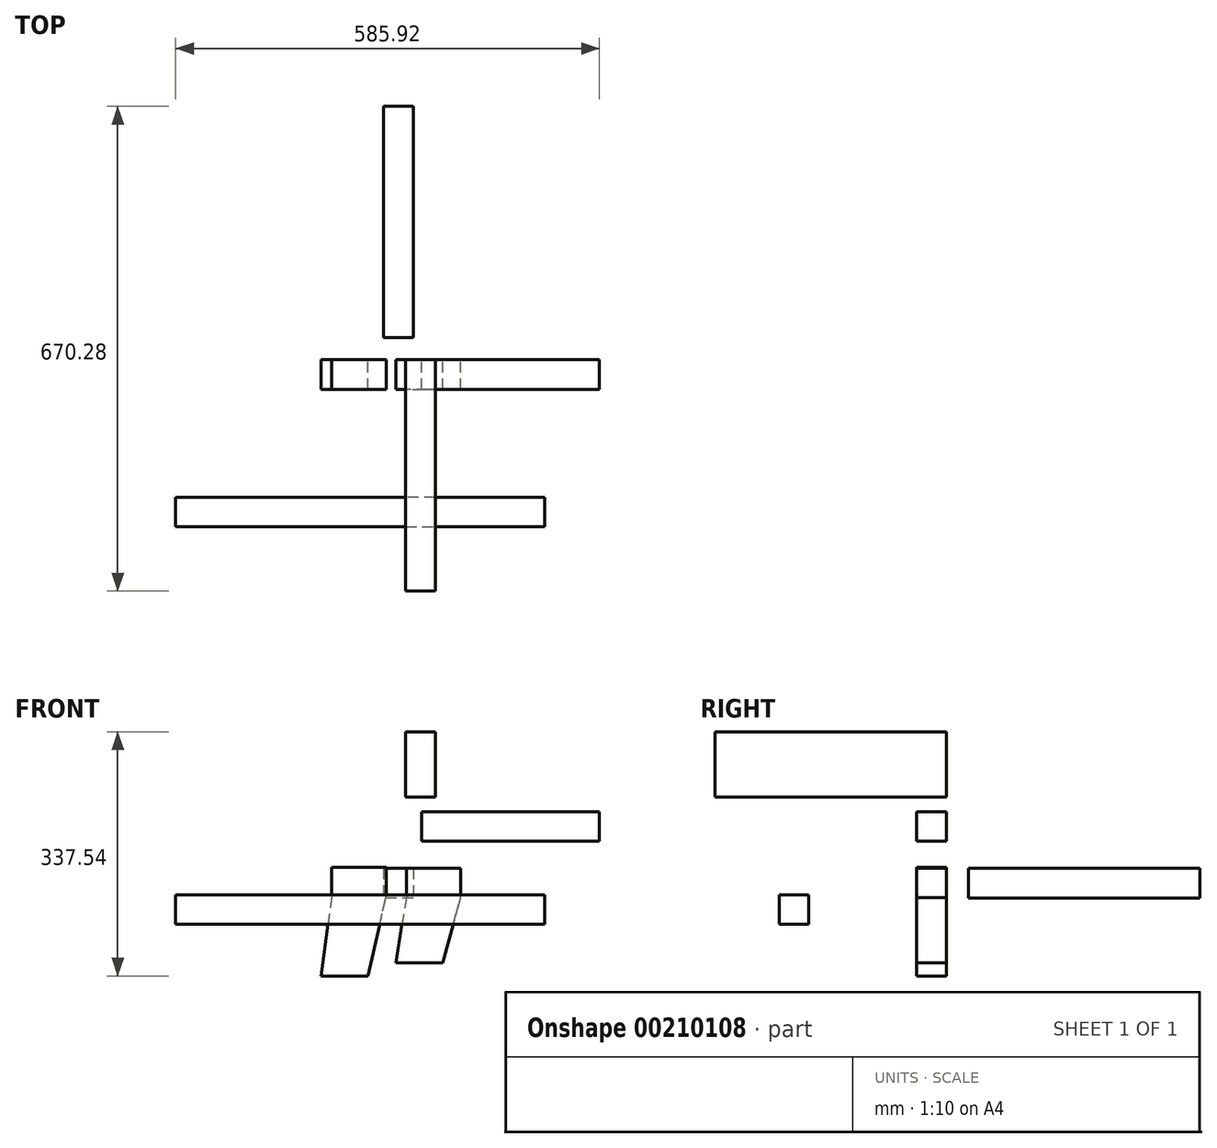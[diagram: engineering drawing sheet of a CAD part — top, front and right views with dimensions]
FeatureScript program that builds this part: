
annotation { "Feature Type Name" : "Feature", "Feature Type Description" : "" }
export const myFeature = defineFeature(function(context is Context, id is Id, definition is map)
    precondition{}
    {
        {
            var Q0;
            Q0=qCreatedBy(makeId("Front.planeOp"),FACE);
            var sketch = newSketch(context, id + "F0", { "sketchPlane" : qUnion([Q0])});
            skLineSegment(sketch, "E0", {"start": v(-71.59, 78.64) * mm, "end": v(-71.59, 37.64) * mm});
            skLineSegment(sketch, "E1", {"start": v(-71.59, 37.64) * mm, "end": v(-86.59, -71.36) * mm});
            skLineSegment(sketch, "E2", {"start": v(-86.59, -71.36) * mm, "end": v(-21.65, -71.36) * mm});
            skLineSegment(sketch, "E3", {"start": v(-21.65, -71.36) * mm, "end": v(3.41, 37.64) * mm});
            skLineSegment(sketch, "E4", {"start": v(3.41, 37.64) * mm, "end": v(3.41, 78.64) * mm});
            skLineSegment(sketch, "E5", {"start": v(3.41, 78.64) * mm, "end": v(-71.59, 78.64) * mm});
            skSolve(sketch);
        }
        {
            var Q0;
            Q0=qSketchRegion(id+"F0",true);
            extrude(context, id + "F1", {"entities" : qUnion([Q0]), "depth" : 41 * mm});
        }
        {
            var Q0;
            Q0=qCreatedBy(makeId("Front.planeOp"),FACE);
            var sketch = newSketch(context, id + "F2", { "sketchPlane" : qUnion([Q0])});
            skLineSegment(sketch, "E6", {"start": v(52.4, 155.86) * mm, "end": v(52.4, 114.86) * mm});
            skLineSegment(sketch, "E7", {"start": v(52.4, 114.86) * mm, "end": v(298.4, 114.86) * mm});
            skLineSegment(sketch, "E8", {"start": v(298.4, 114.86) * mm, "end": v(298.4, 155.86) * mm});
            skLineSegment(sketch, "E9", {"start": v(298.4, 155.86) * mm, "end": v(52.4, 155.86) * mm});
            skSolve(sketch);
        }
        {
            var Q0;
            Q0=qSketchRegion(id+"F2",true);
            extrude(context, id + "F3", {"entities" : qUnion([Q0]), "depth" : 41 * mm});
        }
        {
            var Q0;
            Q0=qCreatedBy(makeId("Right.planeOp"),FACE);
            var sketch = newSketch(context, id + "F4", { "sketchPlane" : qUnion([Q0])});
            skLineSegment(sketch, "E10", {"start": v(30.28, 77.41) * mm, "end": v(30.28, 36.41) * mm});
            skLineSegment(sketch, "E11", {"start": v(30.28, 36.41) * mm, "end": v(350.28, 36.41) * mm});
            skLineSegment(sketch, "E12", {"start": v(350.28, 36.41) * mm, "end": v(350.28, 77.41) * mm});
            skLineSegment(sketch, "E13", {"start": v(350.28, 77.41) * mm, "end": v(30.28, 77.41) * mm});
            skSolve(sketch);
        }
        {
            var Q0;
            Q0=qSketchRegion(id+"F4",true);
            extrude(context, id + "F5", {"entities" : qUnion([Q0]), "depth" : 41 * mm});
        }
        {
            var Q0;
            Q0=qCreatedBy(makeId("Top.planeOp"),FACE);
            var sketch = newSketch(context, id + "F6", { "sketchPlane" : qUnion([Q0])});
            skLineSegment(sketch, "E14", {"start": v(-287.52, -190.26) * mm, "end": v(-287.52, -231.26) * mm});
            skLineSegment(sketch, "E15", {"start": v(-287.52, -231.26) * mm, "end": v(222.48, -231.26) * mm});
            skLineSegment(sketch, "E16", {"start": v(222.48, -231.26) * mm, "end": v(222.48, -190.26) * mm});
            skLineSegment(sketch, "E17", {"start": v(222.48, -190.26) * mm, "end": v(-287.52, -190.26) * mm});
            skSolve(sketch);
        }
        {
            var Q0;
            Q0=makeQuery(id+"F6.imprint","IMPRINT",FACE,{"disambiguationData":[TD([[makeQuery(id+"F6.imprint","IMPRINT",EDGE,{"derivedFrom":sQuery(id+"F6.wireOp",EDGE,"E14")}),1.0]])]});
            extrude(context, id + "F7", {"entities" : qUnion([Q0]), "depth" : 41 * mm});
        }
        {
            var Q0;
            Q0=qCreatedBy(makeId("Front.planeOp"),FACE);
            var sketch = newSketch(context, id + "F8", { "sketchPlane" : qUnion([Q0])});
            skLineSegment(sketch, "E18", {"start": v(71.46, 266.18) * mm, "end": v(30.46, 266.18) * mm});
            skLineSegment(sketch, "E19", {"start": v(30.46, 266.18) * mm, "end": v(30.46, 176.18) * mm});
            skLineSegment(sketch, "E20", {"start": v(30.46, 176.18) * mm, "end": v(71.46, 176.18) * mm});
            skLineSegment(sketch, "E21", {"start": v(71.46, 176.18) * mm, "end": v(71.46, 266.18) * mm});
            skSolve(sketch);
        }
        {
            var Q0;
            Q0=makeQuery(id+"F8.imprint","IMPRINT",FACE,{"disambiguationData":[TD([[makeQuery(id+"F8.imprint","IMPRINT",EDGE,{"derivedFrom":sQuery(id+"F8.wireOp",EDGE,"E18")}),1.0]])]});
            extrude(context, id + "F9", {"entities" : qUnion([Q0]), "depth" : 320 * mm});
        }
        {
            var Q0;
            Q0=qCreatedBy(makeId("Front.planeOp"),FACE);
            var sketch = newSketch(context, id + "F10", { "sketchPlane" : qUnion([Q0])});
            skLineSegment(sketch, "E22", {"start": v(31.74, 77.9) * mm, "end": v(31.74, 36.9) * mm});
            skLineSegment(sketch, "E23", {"start": v(31.74, 36.9) * mm, "end": v(16.74, -53.1) * mm});
            skLineSegment(sketch, "E24", {"start": v(16.74, -53.1) * mm, "end": v(81.68, -53.1) * mm});
            skLineSegment(sketch, "E25", {"start": v(81.68, -53.1) * mm, "end": v(106.74, 36.9) * mm});
            skLineSegment(sketch, "E26", {"start": v(106.74, 36.9) * mm, "end": v(106.74, 77.9) * mm});
            skLineSegment(sketch, "E27", {"start": v(106.74, 77.9) * mm, "end": v(31.74, 77.9) * mm});
            skSolve(sketch);
        }
        {
            var Q0;
            Q0 = qSketchRegion(id + "F10", true);
            extrude(context, id + "F11", {"entities" : qUnion([Q0]), "depth" : 41 * mm});
        }
    });
